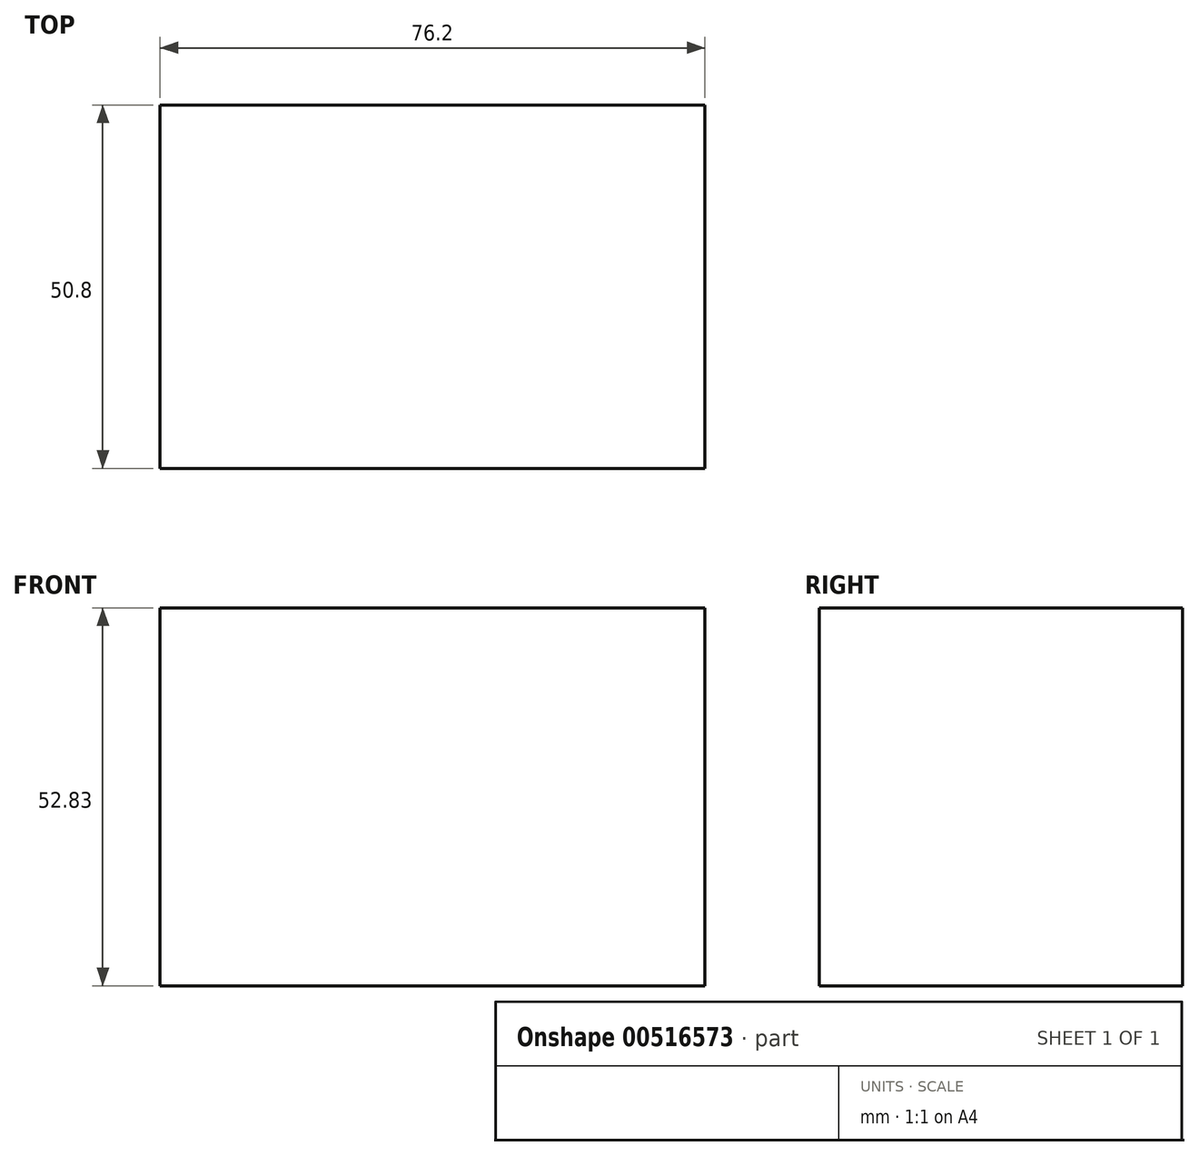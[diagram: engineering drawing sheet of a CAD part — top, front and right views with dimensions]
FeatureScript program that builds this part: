
annotation { "Feature Type Name" : "Feature", "Feature Type Description" : "" }
export const myFeature = defineFeature(function(context is Context, id is Id, definition is map)
    precondition{}
    {
        {
            var Q0;
            Q0=qCreatedBy(makeId("Top.planeOp"),FACE);
            var sketch = newSketch(context, id + "F0", { "sketchPlane" : qUnion([Q0])});
            skLineSegment(sketch, "E0.bottom", {"start": v(-38.1, -25.4) * mm, "end": v(38.1, -25.4) * mm});
            skLineSegment(sketch, "E0.top", {"start": v(-38.1, 25.4) * mm, "end": v(38.1, 25.4) * mm});
            skLineSegment(sketch, "E0.left", {"start": v(-38.1, -25.4) * mm, "end": v(-38.1, 25.4) * mm});
            skLineSegment(sketch, "E0.right", {"start": v(38.1, -25.4) * mm, "end": v(38.1, 25.4) * mm});
            skSolve(sketch);
        }
        {
            var Q0;
            Q0 = qSketchRegion(id + "F0", true);
            extrude(context, id + "F1", {"entities" : qUnion([Q0]), "depth" : 52.83 * mm, "offsetDistance" : 25.4 * mm});
        }
    });
